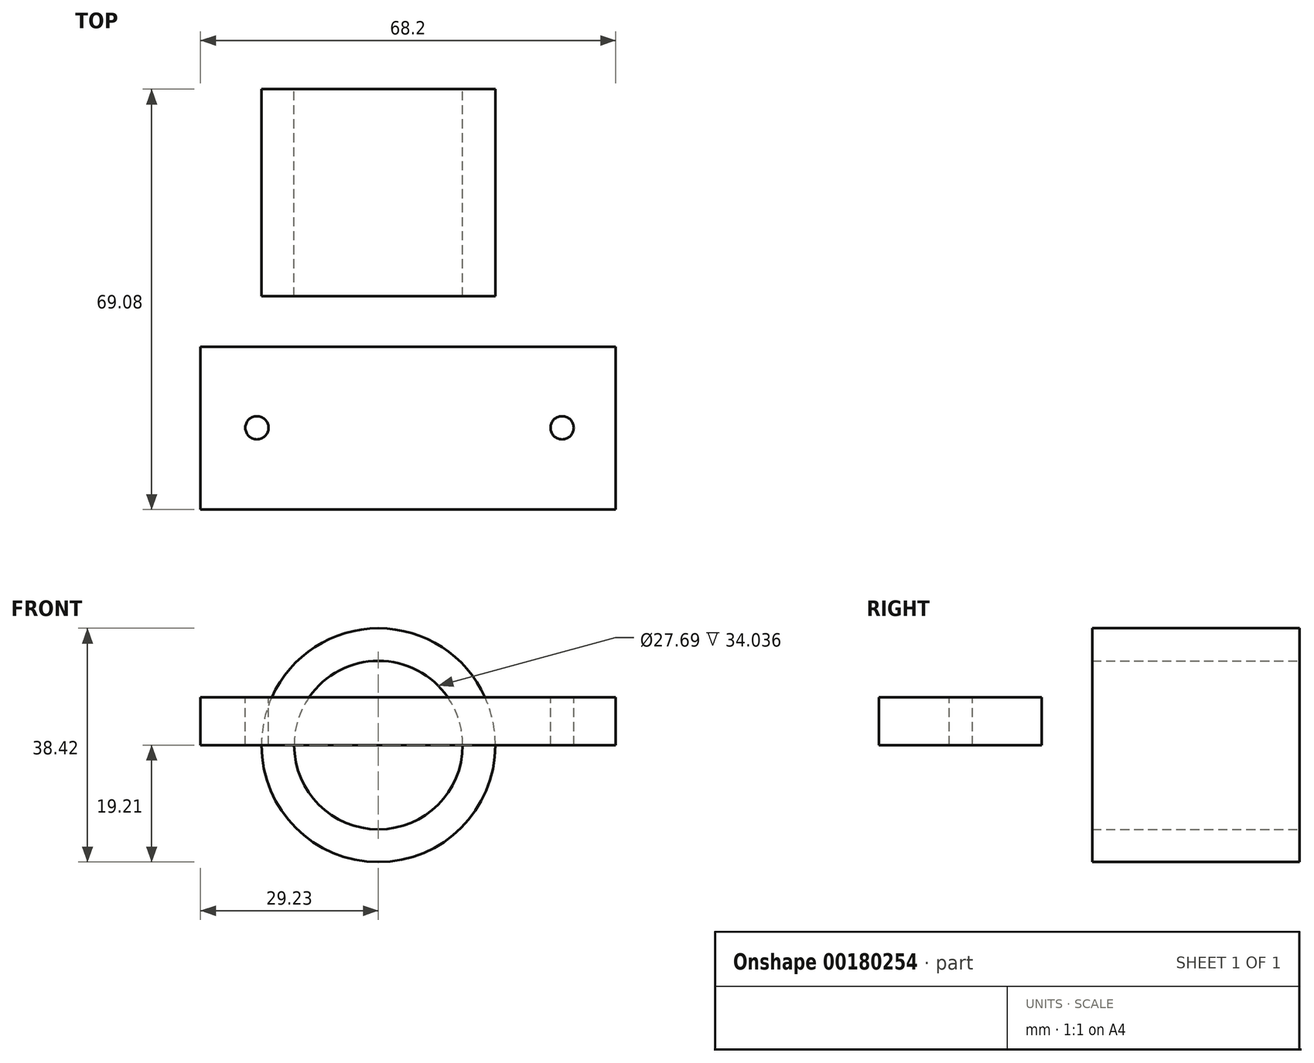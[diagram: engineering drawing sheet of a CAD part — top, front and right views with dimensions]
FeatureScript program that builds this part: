
annotation { "Feature Type Name" : "Feature", "Feature Type Description" : "" }
export const myFeature = defineFeature(function(context is Context, id is Id, definition is map)
    precondition{}
    {
        {
            var Q0;
            Q0=qCreatedBy(makeId("Top.planeOp"),FACE);
            var sketch = newSketch(context, id + "F0", { "sketchPlane" : qUnion([Q0])});
            skLineSegment(sketch, "E0.bottom", {"start": v(38.97, -69.08) * mm, "end": v(-29.23, -69.08) * mm});
            skLineSegment(sketch, "E0.top", {"start": v(38.97, -42.35) * mm, "end": v(-29.23, -42.35) * mm});
            skLineSegment(sketch, "E0.left", {"start": v(38.97, -69.08) * mm, "end": v(38.97, -42.35) * mm});
            skLineSegment(sketch, "E0.right", {"start": v(-29.23, -69.08) * mm, "end": v(-29.23, -42.35) * mm});
            skSolve(sketch);
        }
        {
            var Q0;
            Q0=makeQuery(id+"F0.imprint","IMPRINT",FACE,{"disambiguationData":[TD([[makeQuery(id+"F0.imprint","IMPRINT",EDGE,{"derivedFrom":sQuery(id+"F0.wireOp",EDGE,"E0.bottom")}),-1.0]])]});
            extrude(context, id + "F1", {"entities" : qUnion([Q0]), "depth" : 7.87 * mm});
        }
        {
            var Q0;
            Q0=makeQuery(id+"F1.opExtrude","CAP_FACE",FACE,{"disambiguationData":[OSD([sQuery(id+"F0.wireOp",EDGE,"E0.bottom"),sQuery(id+"F0.wireOp",EDGE,"E0.top"),sQuery(id+"F0.wireOp",EDGE,"E0.left"),sQuery(id+"F0.wireOp",EDGE,"E0.right")])],"isStart":false});
            var sketch = newSketch(context, id + "F2", { "sketchPlane" : qUnion([Q0])});
            skCircle(sketch, "E1", {"center": v(-19.95, -55.63) * mm, "radius": 1.9 * mm});
            skCircle(sketch, "E2", {"center": v(30.17, -55.63) * mm, "radius": 1.9 * mm});
            skSolve(sketch);
        }
        {
            var Q0;
            Q0 = qSketchRegion(id + "F2", true);
            extrude(context, id + "F3", {"entities" : qUnion([Q0]), "operationType" : NewBodyOperationType.REMOVE, "oppositeDirection" : true, "depth" : 25.4 * mm});
        }
        {
            var Q0;
            Q0=qCreatedBy(makeId("Front.planeOp"),FACE);
            var sketch = newSketch(context, id + "F4", { "sketchPlane" : qUnion([Q0])});
            skCircle(sketch, "E3", {"center": v(0, 0) * mm, "radius": 19.2 * mm});
            skCircle(sketch, "E4", {"center": v(0, 0) * mm, "radius": 13.84 * mm});
            skSolve(sketch);
        }
        {
            var Q0;
            Q0 = qSketchRegion(id + "F4", true);
            extrude(context, id + "F5", {"entities" : qUnion([Q0]), "depth" : 34.04 * mm});
        }
    });
